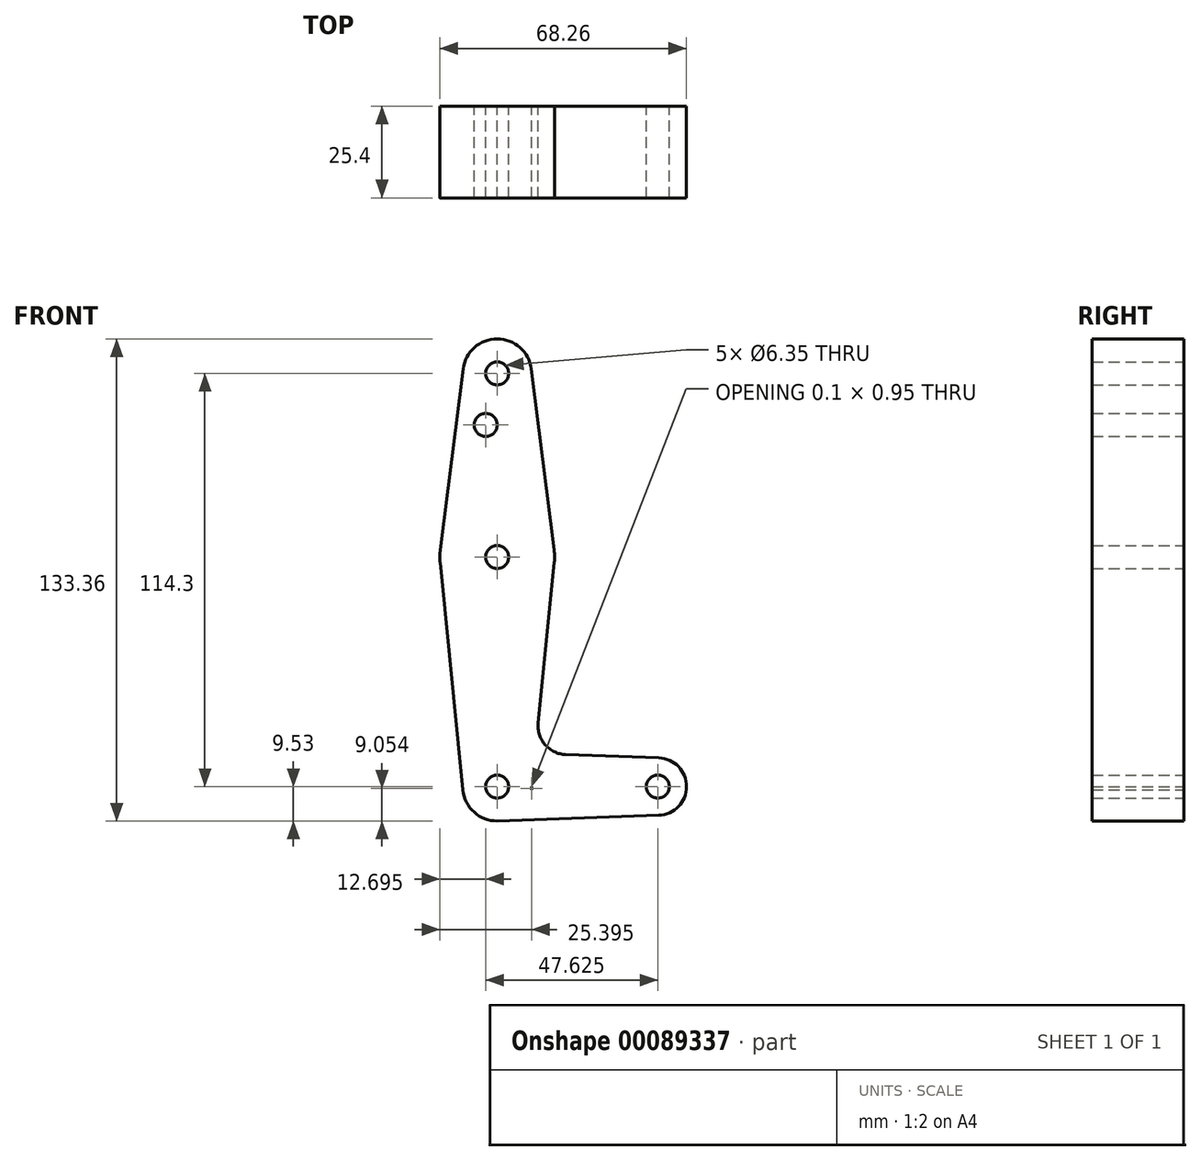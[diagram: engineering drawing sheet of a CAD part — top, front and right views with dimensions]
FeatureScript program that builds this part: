
annotation { "Feature Type Name" : "Feature", "Feature Type Description" : "" }
export const myFeature = defineFeature(function(context is Context, id is Id, definition is map)
    precondition{}
    {
        {
            var Q0;
            Q0=qCreatedBy(makeId("Front.planeOp"),FACE);
            var sketch = newSketch(context, id + "F0", { "sketchPlane" : qUnion([Q0])});
            skCircle(sketch, "E0", {"center": v(0, 114.3) * mm, "radius": 9.53 * mm});
            skCircle(sketch, "E1", {"center": v(0, 63.5) * mm, "radius": 15.88 * mm});
            skCircle(sketch, "E2", {"center": v(0, 0) * mm, "radius": 9.53 * mm});
            skCircle(sketch, "E3", {"center": v(44.45, 0) * mm, "radius": 7.94 * mm});
            skLineSegment(sketch, "E4", {"start": v(0, 114.3) * mm, "end": v(0, 0) * mm});
            skLineSegment(sketch, "E5", {"start": v(0, 0) * mm, "end": v(44.45, 0) * mm});
            skLineSegment(sketch, "E6", {"start": v(-9.45, 115.5) * mm, "end": v(-15.75, 65.48) * mm});
            skLineSegment(sketch, "E7", {"start": v(9.45, 115.5) * mm, "end": v(15.75, 65.48) * mm});
            skLineSegment(sketch, "E8", {"start": v(-15.8, 61.91) * mm, "end": v(-9.48, -0.95) * mm});
            skLineSegment(sketch, "E9", {"start": v(15.8, 61.91) * mm, "end": v(9.48, -0.95) * mm});
            skLineSegment(sketch, "E10", {"start": v(0.34, 9.52) * mm, "end": v(44.73, 7.93) * mm});
            skLineSegment(sketch, "E11", {"start": v(0, -9.53) * mm, "end": v(44.73, -7.93) * mm});
            skArc(sketch, "E12", {"start": v(11.34, 17.6) * mm, "mid": v(13.26, 11.57) * mm, "end": v(18.97, 8.85) * mm});
            skCircle(sketch, "E13", {"center": v(0, 114.3) * mm, "radius": 3.18 * mm});
            skCircle(sketch, "E14", {"center": v(0, 63.5) * mm, "radius": 3.18 * mm});
            skCircle(sketch, "E15", {"center": v(0, 0) * mm, "radius": 3.18 * mm});
            skCircle(sketch, "E16", {"center": v(44.45, 0) * mm, "radius": 3.18 * mm});
            skCircle(sketch, "E17", {"center": v(-3.17, 100.03) * mm, "radius": 3.17 * mm});
            skSolve(sketch);
        }
        {
            var Q0;
            {var subQ7=sQuery(id+"F0.wireOp",EDGE,"E6");Q0=makeQuery(id+"F0.imprint","IMPRINT",FACE,{"disambiguationData":[TD([[makeQuery(id+"F0.imprint","IMPRINT",EDGE,{"derivedFrom":subQ7}),1.0]])]});}
            var Q1;
            {var subQ6=sQuery(id+"F0.wireOp",EDGE,"E7");Q1=makeQuery(id+"F0.imprint","IMPRINT",FACE,{"disambiguationData":[TD([[makeQuery(id+"F0.imprint","IMPRINT",EDGE,{"derivedFrom":subQ6}),-1.0]])]});}
            var Q2;
            {var subQ0=sQuery(id+"F0.wireOp",EDGE,"E1");var subQ1=makeQuery(id+"F0.imprint","INTERSECT",VERTEX,{"derivedFrom":[subQ0,sQuery(id+"F0.wireOp",EDGE,"E7")]});Q2=makeQuery(id+"F0.imprint","IMPRINT",FACE,{"disambiguationData":[TD([[makeQuery(id+"F0.imprint","IMPRINT",EDGE,{"disambiguationData":[TD([[subQ1,-1.0]])],"derivedFrom":subQ0}),1.0]])]});}
            var Q3;
            Q3=makeQuery(id+"F0.imprint","IMPRINT",FACE,{"disambiguationData":[TD([[makeQuery(id+"F0.imprint","IMPRINT",EDGE,{"derivedFrom":sQuery(id+"F0.wireOp",EDGE,"E13")}),-1.0]])]});
            var Q4;
            {var subQ1=sQuery(id+"F0.wireOp",EDGE,"E1");var subQ7=makeQuery(id+"F0.imprint","INTERSECT",VERTEX,{"derivedFrom":[subQ1,sQuery(id+"F0.wireOp",EDGE,"E6")]});Q4=makeQuery(id+"F0.imprint","IMPRINT",FACE,{"disambiguationData":[TD([[makeQuery(id+"F0.imprint","IMPRINT",EDGE,{"disambiguationData":[TD([[subQ7,1.0]])],"derivedFrom":subQ1}),1.0]])]});}
            var Q5;
            {var subQ0=sQuery(id+"F0.wireOp",EDGE,"E8");Q5=makeQuery(id+"F0.imprint","IMPRINT",FACE,{"disambiguationData":[TD([[makeQuery(id+"F0.imprint","IMPRINT",EDGE,{"derivedFrom":subQ0}),1.0]])]});}
            var Q6;
            {var subQ1=sQuery(id+"F0.wireOp",EDGE,"E1");var subQ7=sQuery(id+"F0.wireOp",EDGE,"E9");var subQ9=makeQuery(id+"F0.imprint","INTERSECT",VERTEX,{"derivedFrom":[subQ1,subQ7]});Q6=makeQuery(id+"F0.imprint","IMPRINT",FACE,{"disambiguationData":[TD([[makeQuery(id+"F0.imprint","IMPRINT",EDGE,{"disambiguationData":[TD([[subQ9,1.0]])],"derivedFrom":subQ1}),-1.0]])]});}
            var Q7;
            {var subQ3=sQuery(id+"F0.wireOp",EDGE,"E10");var subQ5=sQuery(id+"F0.wireOp",EDGE,"E3");var subQ6=makeQuery(id+"F0.imprint","INTERSECT",VERTEX,{"derivedFrom":[subQ5,subQ3]});Q7=makeQuery(id+"F0.imprint","IMPRINT",FACE,{"disambiguationData":[TD([[makeQuery(id+"F0.imprint","IMPRINT",EDGE,{"disambiguationData":[TD([[subQ6,-1.0]])],"derivedFrom":subQ5}),-1.0]])]});}
            var Q8;
            {var subQ0=sQuery(id+"F0.wireOp",EDGE,"E9");var subQ1=sQuery(id+"F0.wireOp",EDGE,"E2");var subQ2=makeQuery(id+"F0.imprint","INTERSECT",VERTEX,{"derivedFrom":[subQ1,subQ0]});Q8=makeQuery(id+"F0.imprint","IMPRINT",FACE,{"disambiguationData":[TD([[makeQuery(id+"F0.imprint","IMPRINT",EDGE,{"disambiguationData":[TD([[subQ2,1.0]])],"derivedFrom":subQ1}),-1.0]])]});}
            var Q9;
            {var subQ0=sQuery(id+"F0.wireOp",EDGE,"E10");var subQ1=sQuery(id+"F0.wireOp",EDGE,"E2");var subQ2=makeQuery(id+"F0.imprint","INTERSECT",VERTEX,{"derivedFrom":[subQ1,subQ0]});Q9=makeQuery(id+"F0.imprint","IMPRINT",FACE,{"disambiguationData":[TD([[makeQuery(id+"F0.imprint","IMPRINT",EDGE,{"disambiguationData":[TD([[subQ2,1.0]])],"derivedFrom":subQ1}),-1.0]])]});}
            var Q10;
            {var subQ1=sQuery(id+"F0.wireOp",EDGE,"E2");var subQ8=makeQuery(id+"F0.imprint","INTERSECT",VERTEX,{"derivedFrom":[subQ1,sQuery(id+"F0.wireOp",EDGE,"E10")]});Q10=makeQuery(id+"F0.imprint","IMPRINT",FACE,{"disambiguationData":[TD([[makeQuery(id+"F0.imprint","IMPRINT",EDGE,{"disambiguationData":[TD([[subQ8,1.0]])],"derivedFrom":subQ1}),1.0]])]});}
            var Q11;
            {var subQ0=sQuery(id+"F0.wireOp",EDGE,"E2");var subQ10=makeQuery(id+"F0.imprint","INTERSECT",VERTEX,{"derivedFrom":[subQ0,sQuery(id+"F0.wireOp",EDGE,"E8")]});Q11=makeQuery(id+"F0.imprint","IMPRINT",FACE,{"disambiguationData":[TD([[makeQuery(id+"F0.imprint","IMPRINT",EDGE,{"disambiguationData":[TD([[subQ10,1.0]])],"derivedFrom":subQ0}),1.0]])]});}
            var Q12;
            Q12=makeQuery(id+"F0.imprint","IMPRINT",FACE,{"disambiguationData":[TD([[makeQuery(id+"F0.imprint","IMPRINT",EDGE,{"derivedFrom":sQuery(id+"F0.wireOp",EDGE,"E16")}),-1.0]])]});
            var Q13;
            {var subQ0=sQuery(id+"F0.wireOp",EDGE,"E12");Q13=makeQuery(id+"F0.imprint","IMPRINT",FACE,{"disambiguationData":[TD([[makeQuery(id+"F0.imprint","IMPRINT",EDGE,{"derivedFrom":subQ0}),-1.0]])]});}
            extrude(context, id + "F1", {"entities" : qUnion([Q0, Q1, Q2, Q3, Q4, Q5, Q6, Q7, Q8, Q9, Q10, Q11, Q12, Q13]), "depth" : 25.4 * mm});
        }
    });
